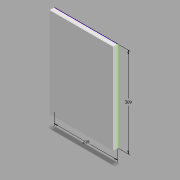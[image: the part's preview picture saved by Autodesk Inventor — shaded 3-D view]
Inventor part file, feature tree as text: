
AUTODESK INVENTOR PART (.ipt)
format: ipt  version: 2022 (Build 260153000, 153)  size: 98,304 bytes
history: native  units: mm
features: extrude x1, sketch x1
ambient origin geometry x8: Origin, YZ Plane, XZ Plane, XY Plane, X Axis, Y Axis, Z Axis, Center Point
bodies: Body1 (feature_tree)
feature tree (2):
  extrude  "Выдавливание2"  Depth=218.0mm
  sketch  "Эскиз1"
